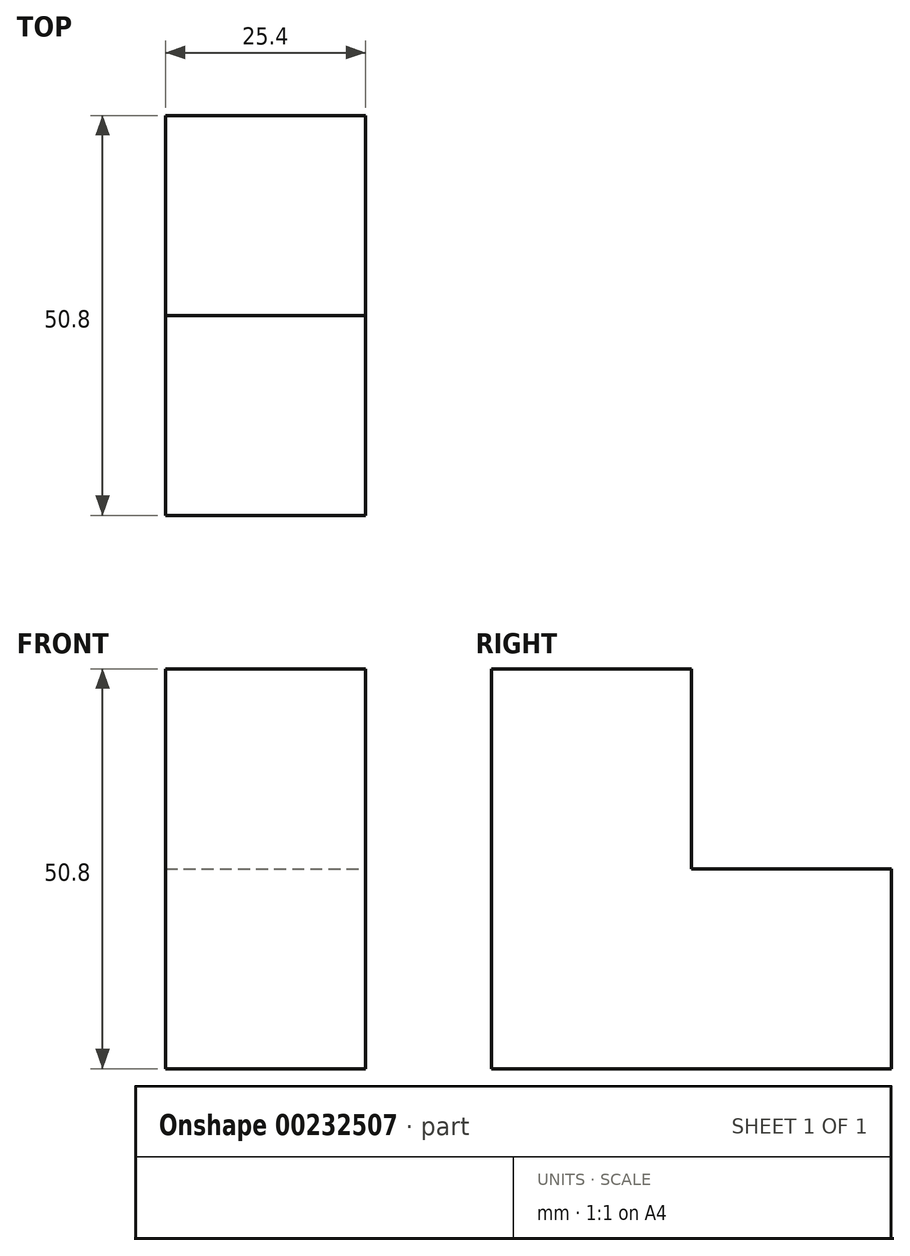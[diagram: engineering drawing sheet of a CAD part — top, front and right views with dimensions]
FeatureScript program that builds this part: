
annotation { "Feature Type Name" : "Feature", "Feature Type Description" : "" }
export const myFeature = defineFeature(function(context is Context, id is Id, definition is map)
    precondition{}
    {
        {
            var Q0;
            Q0=qCreatedBy(makeId("Front.planeOp"),FACE);
            var sketch = newSketch(context, id + "F0", { "sketchPlane" : qUnion([Q0])});
            skLineSegment(sketch, "E0.bottom", {"start": v(-33.26, 26.04) * mm, "end": v(-7.86, 26.04) * mm});
            skLineSegment(sketch, "E0.top", {"start": v(-33.26, 0.64) * mm, "end": v(-7.86, 0.64) * mm});
            skLineSegment(sketch, "E0.left", {"start": v(-33.26, 26.04) * mm, "end": v(-33.26, 0.64) * mm});
            skLineSegment(sketch, "E0.right", {"start": v(-7.86, 26.04) * mm, "end": v(-7.86, 0.64) * mm});
            skSolve(sketch);
        }
        {
            var Q0;
            Q0=makeQuery(id+"F0.imprint","IMPRINT",FACE,{"disambiguationData":[TD([[makeQuery(id+"F0.imprint","IMPRINT",EDGE,{"derivedFrom":sQuery(id+"F0.wireOp",EDGE,"E0.bottom")}),-1.0]])]});
            extrude(context, id + "F1", {"entities" : qUnion([Q0]), "depth" : 50.8 * mm});
        }
        {
            var Q0;
            Q0=makeQuery(id+"F1.opExtrude","SWEPT_FACE",FACE,{"disambiguationData":[OSD([sQuery(id+"F0.wireOp",EDGE,"E0.bottom")])]});
            var sketch = newSketch(context, id + "F2", { "sketchPlane" : qUnion([Q0])});
            skLineSegment(sketch, "E1.bottom", {"start": v(-33.26, -25.4) * mm, "end": v(-7.86, -25.4) * mm});
            skLineSegment(sketch, "E1.top", {"start": v(-33.26, -50.8) * mm, "end": v(-7.86, -50.8) * mm});
            skLineSegment(sketch, "E1.left", {"start": v(-33.26, -25.4) * mm, "end": v(-33.26, -50.8) * mm});
            skLineSegment(sketch, "E1.right", {"start": v(-7.86, -25.4) * mm, "end": v(-7.86, -50.8) * mm});
            skSolve(sketch);
        }
        {
            var Q0;
            Q0=makeQuery(id+"F2.imprint","IMPRINT",FACE,{"disambiguationData":[TD([[makeQuery(id+"F2.imprint","IMPRINT",EDGE,{"derivedFrom":sQuery(id+"F2.wireOp",EDGE,"E1.bottom")}),-1.0]])]});
            extrude(context, id + "F3", {"entities" : qUnion([Q0]), "operationType" : NewBodyOperationType.ADD, "depth" : 25.4 * mm});
        }
    });
